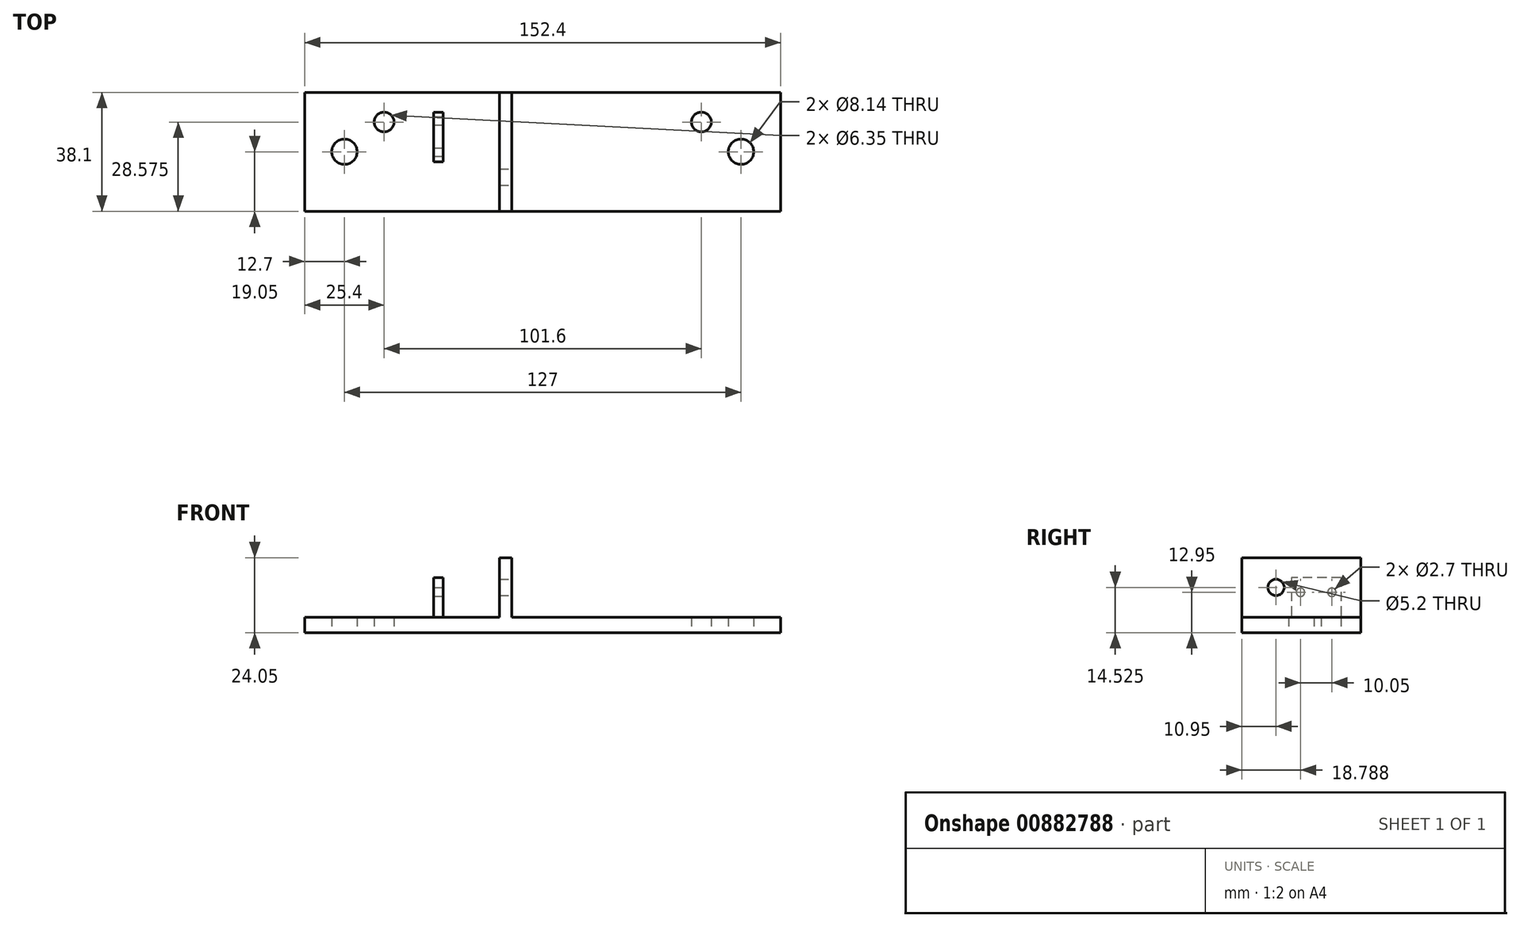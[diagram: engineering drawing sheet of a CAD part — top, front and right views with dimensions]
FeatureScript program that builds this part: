
annotation { "Feature Type Name" : "Feature", "Feature Type Description" : "" }
export const myFeature = defineFeature(function(context is Context, id is Id, definition is map)
    precondition{}
    {
        {
            var Q0;
            Q0=qCreatedBy(makeId("Top.planeOp"),FACE);
            var sketch = newSketch(context, id + "F0", { "sketchPlane" : qUnion([Q0])});
            skLineSegment(sketch, "E0.bottom", {"start": v(76.2, -19.05) * mm, "end": v(-76.2, -19.05) * mm});
            skLineSegment(sketch, "E0.top", {"start": v(76.2, 19.05) * mm, "end": v(-76.2, 19.05) * mm});
            skLineSegment(sketch, "E0.left", {"start": v(76.2, -19.05) * mm, "end": v(76.2, 19.05) * mm});
            skLineSegment(sketch, "E0.right", {"start": v(-76.2, -19.05) * mm, "end": v(-76.2, 19.05) * mm});
            skPoint(sketch, "E0.middle", {"position": v(0, 0) * mm});
            skCircle(sketch, "E1", {"center": v(-63.5, 0) * mm, "radius": 4.07 * mm});
            skCircle(sketch, "E2", {"center": v(63.5, 0) * mm, "radius": 4.07 * mm});
            skLineSegment(sketch, "E3", {"start": v(0, 19.05) * mm, "end": v(0, -19.05) * mm});
            skCircle(sketch, "E4", {"center": v(-50.8, 9.52) * mm, "radius": 3.18 * mm});
            skCircle(sketch, "E5", {"center": v(50.8, 9.52) * mm, "radius": 3.18 * mm});
            skSolve(sketch);
        }
        {
            var Q0;
            Q0=qSketchRegion(id+"F0",true);
            extrude(context, id + "F1", {"entities" : qUnion([Q0]), "depth" : 5 * mm, "offsetDistance" : 25.4 * mm});
        }
        {
            var Q0;
            Q0=makeQuery(id+"F1.opExtrude","CAP_FACE",FACE,{"disambiguationData":[OSD([sQuery(id+"F0.wireOp",EDGE,"E0.bottom"),sQuery(id+"F0.wireOp",EDGE,"E0.top"),sQuery(id+"F0.wireOp",EDGE,"E0.left"),sQuery(id+"F0.wireOp",EDGE,"E0.right"),sQuery(id+"F0.wireOp",EDGE,"E1"),sQuery(id+"F0.wireOp",EDGE,"E2"),sQuery(id+"F0.wireOp",EDGE,"E4"),sQuery(id+"F0.wireOp",EDGE,"E5")])],"isStart":false});
            var sketch = newSketch(context, id + "F2", { "sketchPlane" : qUnion([Q0])});
            skLineSegment(sketch, "E6.bottom", {"start": v(-13.89, 19.05) * mm, "end": v(-9.9, 19.05) * mm});
            skLineSegment(sketch, "E6.top", {"start": v(-13.89, -19.05) * mm, "end": v(-9.89, -19.05) * mm});
            skLineSegment(sketch, "E6.left", {"start": v(-13.89, 19.05) * mm, "end": v(-13.89, -19.05) * mm});
            skLineSegment(sketch, "E6.right", {"start": v(-9.9, 19.05) * mm, "end": v(-9.89, -19.05) * mm});
            skLineSegment(sketch, "E7", {"start": v(-76.2, 0) * mm, "end": v(76.2, 0) * mm});
            skSolve(sketch);
        }
        {
            var Q0;
            Q0=qSketchRegion(id+"F2",true);
            extrude(context, id + "F3", {"entities" : qUnion([Q0]), "operationType" : NewBodyOperationType.ADD, "depth" : 19.05 * mm, "offsetDistance" : 25.4 * mm});
        }
        {
            var Q0;
            {var subQ0=sQuery(id+"F0.wireOp",EDGE,"E1");var subQ1=sQuery(id+"F0.wireOp",EDGE,"E0.top");var subQ2=sQuery(id+"F0.wireOp",EDGE,"E0.right");var subQ3=sQuery(id+"F0.wireOp",EDGE,"E0.bottom");var subQ4=sQuery(id+"F0.wireOp",EDGE,"E4");Q0=makeQuery(id+"F3.boolean.opBoolean","SPLIT",FACE,{"disambiguationData":[TD([makeQuery(id+"F1.opExtrude","SWEPT_FACE",FACE,{"disambiguationData":[OSD([subQ2])]})])],"derivedFrom":makeQuery(id+"F1.opExtrude","CAP_FACE",FACE,{"disambiguationData":[OSD([subQ3,subQ1,sQuery(id+"F0.wireOp",EDGE,"E0.left"),subQ2,subQ0,sQuery(id+"F0.wireOp",EDGE,"E2"),subQ4,sQuery(id+"F0.wireOp",EDGE,"E5")])],"isStart":false})});}
            var sketch = newSketch(context, id + "F4", { "sketchPlane" : qUnion([Q0])});
            skLineSegment(sketch, "E8.bottom", {"start": v(-34.93, 12.7) * mm, "end": v(-31.93, 12.7) * mm});
            skLineSegment(sketch, "E8.top", {"start": v(-34.93, -3.18) * mm, "end": v(-31.93, -3.18) * mm});
            skLineSegment(sketch, "E8.left", {"start": v(-34.93, 12.7) * mm, "end": v(-34.93, -3.18) * mm});
            skLineSegment(sketch, "E8.right", {"start": v(-31.93, 12.7) * mm, "end": v(-31.93, -3.18) * mm});
            skSolve(sketch);
        }
        {
            var Q0;
            Q0=qSketchRegion(id+"F4",true);
            extrude(context, id + "F5", {"entities" : qUnion([Q0]), "operationType" : NewBodyOperationType.ADD, "depth" : 12.7 * mm, "offsetDistance" : 25.4 * mm});
        }
        {
            var Q0;
            Q0=makeQuery(id+"F3.opExtrude","SWEPT_FACE",FACE,{"disambiguationData":[OSD([sQuery(id+"F2.wireOp",EDGE,"E6.right")])]});
            var sketch = newSketch(context, id + "F6", { "sketchPlane" : qUnion([Q0])});
            skCircle(sketch, "E9", {"center": v(-8.1, 14.53) * mm, "radius": 2.6 * mm});
            skLineSegment(sketch, "E10", {"start": v(-8.1, 14.53) * mm, "end": v(37.44, 14.53) * mm});
            skLineSegment(sketch, "E11", {"start": v(0, 24.05) * mm, "end": v(0, 5) * mm});
            skLineSegment(sketch, "E12", {"start": v(-19.05, 14.53) * mm, "end": v(19.05, 14.53) * mm});
            skSolve(sketch);
        }
        {
            var Q0;
            Q0=qSketchRegion(id+"F6",true);
            extrude(context, id + "F7", {"entities" : qUnion([Q0]), "operationType" : NewBodyOperationType.REMOVE, "endBound" : BoundingType.UP_TO_NEXT, "oppositeDirection" : true, "depth" : 25.4 * mm, "offsetDistance" : 25.4 * mm});
        }
        {
            var Q0;
            Q0=makeQuery(id+"F5.opExtrude","SWEPT_FACE",FACE,{"disambiguationData":[OSD([sQuery(id+"F4.wireOp",EDGE,"E8.left")])]});
            var sketch = newSketch(context, id + "F8", { "sketchPlane" : qUnion([Q0])});
            skCircle(sketch, "E13", {"center": v(-9.79, 12.95) * mm, "radius": 1.35 * mm});
            skCircle(sketch, "E14", {"center": v(0.26, 12.95) * mm, "radius": 1.35 * mm});
            skLineSegment(sketch, "E15", {"start": v(-4.76, 17.7) * mm, "end": v(-4.76, 5) * mm});
            skSolve(sketch);
        }
        {
            var Q0;
            Q0 = qSketchRegion(id + "F8", true);
            extrude(context, id + "F9", {"entities" : qUnion([Q0]), "operationType" : NewBodyOperationType.REMOVE, "endBound" : BoundingType.UP_TO_NEXT, "oppositeDirection" : true, "depth" : 25.4 * mm, "offsetDistance" : 25.4 * mm});
        }
    });
